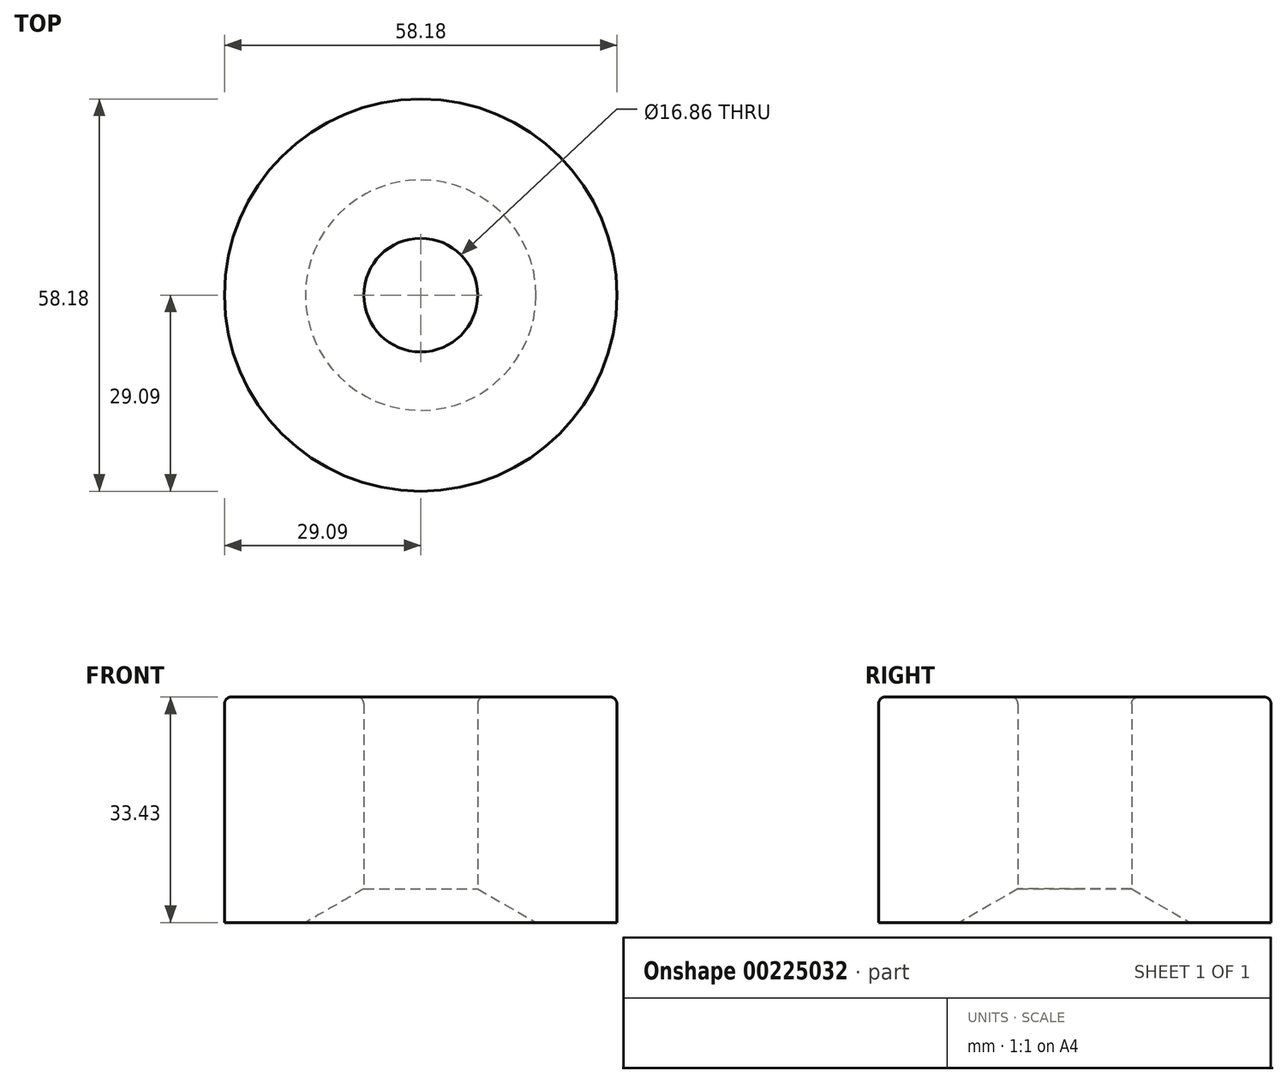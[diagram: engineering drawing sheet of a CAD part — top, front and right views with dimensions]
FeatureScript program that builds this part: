
annotation { "Feature Type Name" : "Feature", "Feature Type Description" : "" }
export const myFeature = defineFeature(function(context is Context, id is Id, definition is map)
    precondition{}
    {
        {
            var Q0;
            Q0=qCreatedBy(makeId("Front.planeOp"),FACE);
            var sketch = newSketch(context, id + "F0", { "sketchPlane" : qUnion([Q0])});
            skLineSegment(sketch, "E0", {"start": v(0, 0) * mm, "end": v(0, 68.64) * mm, "construction": true});
            skLineSegment(sketch, "E1", {"start": v(0, 0) * mm, "end": v(107.22, 0) * mm, "construction": true});
            skLineSegment(sketch, "E2", {"start": v(8.43, 52.24) * mm, "end": v(8.43, 23.81) * mm});
            skLineSegment(sketch, "E3", {"start": v(8.43, 23.81) * mm, "end": v(17.09, 18.81) * mm});
            skLineSegment(sketch, "E4", {"start": v(17.09, 18.81) * mm, "end": v(29.09, 18.81) * mm});
            skLineSegment(sketch, "E5", {"start": v(29.09, 18.81) * mm, "end": v(29.09, 52.24) * mm});
            skLineSegment(sketch, "E6", {"start": v(29.09, 52.24) * mm, "end": v(8.43, 52.24) * mm});
            skSolve(sketch);
        }
        {
            var Q0;
            Q0=makeQuery(id+"F0.imprint","IMPRINT",FACE,{"disambiguationData":[TD([[makeQuery(id+"F0.imprint","IMPRINT",EDGE,{"derivedFrom":sQuery(id+"F0.wireOp",EDGE,"E2")}),1.0]])]});
            var Q1;
            Q1=sQuery(id+"F0.wireOp",EDGE,"E0");
            revolve(context, id + "F1", {"entities" : qUnion([Q0]), "axis" : qUnion([Q1]), "revolveType" : RevolveType.FULL});
        }
        {
            var Q0;
            Q0=makeQuery(id+"F1.opRevolve","SWEPT_EDGE",EDGE,{"disambiguationData":[OSD([sQuery(id+"F0.wireOp",EDGE,"E5"),sQuery(id+"F0.wireOp",EDGE,"E6")])]});
            var Q1;
            Q1=makeQuery(id+"F1.opRevolve","SWEPT_EDGE",EDGE,{"disambiguationData":[OSD([sQuery(id+"F0.wireOp",EDGE,"E2"),sQuery(id+"F0.wireOp",EDGE,"E6")])]});
            fillet(context, id + "F2", {"entities" : qUnion([Q0, Q1]), "radius" : 1 * mm, "tangentPropagation" : true, "allowEdgeOverflow" : false});
        }
    });
